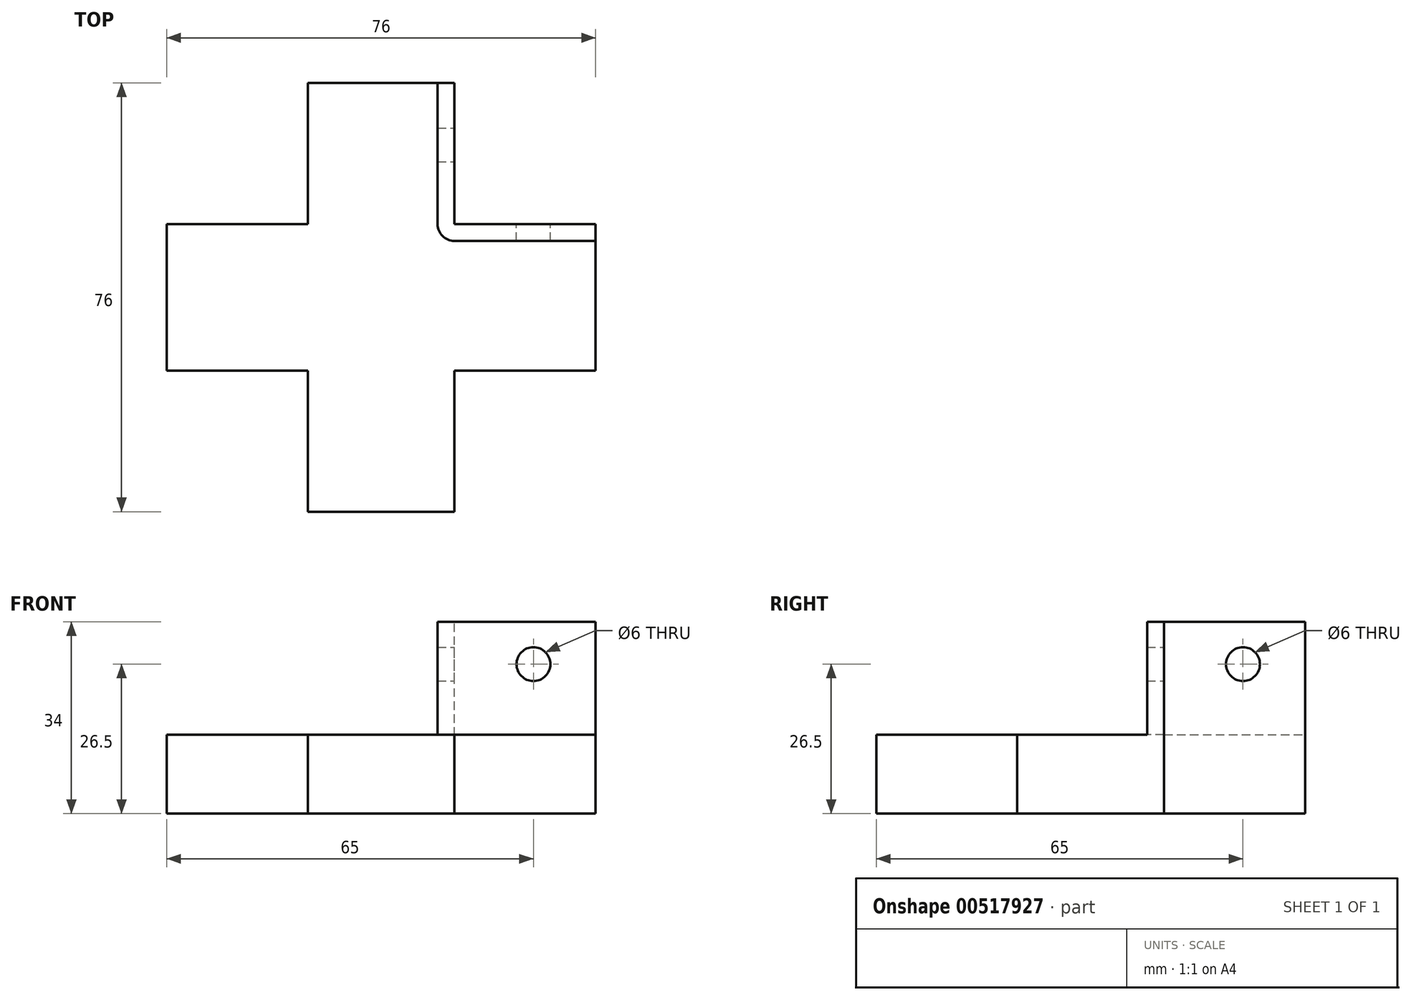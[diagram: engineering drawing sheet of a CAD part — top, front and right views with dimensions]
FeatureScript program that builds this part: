
annotation { "Feature Type Name" : "Feature", "Feature Type Description" : "" }
export const myFeature = defineFeature(function(context is Context, id is Id, definition is map)
    precondition{}
    {
        {
            assignVariable(context, id + "F0", {"name" : "wall_height", "anyValue" : 20});
        }
        {
            var Q0;
            Q0=qCreatedBy(makeId("Top.planeOp"),FACE);
            var sketch = newSketch(context, id + "F1", { "sketchPlane" : qUnion([Q0])});
            skCircle(sketch, "E0", {"center": v(0, 0) * mm, "radius": 15.9 * mm, "construction": true});
            skSolve(sketch);
        }
        {
            var Q0;
            Q0=qCreatedBy(makeId("Top.planeOp"),FACE);
            var sketch = newSketch(context, id + "F2", { "sketchPlane" : qUnion([Q0])});
            skLineSegment(sketch, "E1", {"start": v(-13, 13) * mm, "end": v(-13, 38) * mm});
            skLineSegment(sketch, "E2", {"start": v(-13, 38) * mm, "end": v(13, 38) * mm});
            skLineSegment(sketch, "E3", {"start": v(13, 38) * mm, "end": v(13, 13) * mm});
            skLineSegment(sketch, "E4.1.0", {"start": v(-13, -13) * mm, "end": v(-38, -13) * mm});
            skLineSegment(sketch, "E4.1.1", {"start": v(-38, -13) * mm, "end": v(-38, 13) * mm});
            skLineSegment(sketch, "E4.1.2", {"start": v(-38, 13) * mm, "end": v(-13, 13) * mm});
            skLineSegment(sketch, "E4.2.0", {"start": v(13, -13) * mm, "end": v(13, -38) * mm});
            skLineSegment(sketch, "E4.2.1", {"start": v(13, -38) * mm, "end": v(-13, -38) * mm});
            skLineSegment(sketch, "E4.2.2", {"start": v(-13, -38) * mm, "end": v(-13, -13) * mm});
            skLineSegment(sketch, "E4.3.0", {"start": v(13, 13) * mm, "end": v(38, 13) * mm});
            skLineSegment(sketch, "E4.3.1", {"start": v(38, 13) * mm, "end": v(38, -13) * mm});
            skLineSegment(sketch, "E4.3.2", {"start": v(38, -13) * mm, "end": v(13, -13) * mm});
            skPoint(sketch, "E4.center", {"position": v(0, 0) * mm});
            skSolve(sketch);
        }
        {
            var Q0;
            Q0 = qSketchRegion(id + "F2", true);
            extrude(context, id + "F3", {"entities" : qUnion([Q0]), "oppositeDirection" : true, "depth" : 14 * mm, "offsetDistance" : 25 * mm});
        }
        {
            var Q0;
            Q0=qCreatedBy(makeId("Top.planeOp"),FACE);
            var sketch = newSketch(context, id + "F4", { "sketchPlane" : qUnion([Q0])});
            skLineSegment(sketch, "E5", {"start": v(10, 38) * mm, "end": v(10, 10) * mm});
            skLineSegment(sketch, "E6", {"start": v(10, 10) * mm, "end": v(38, 10) * mm});
            skLineSegment(sketch, "E7.0", {"start": v(13, 13) * mm, "end": v(38, 13) * mm});
            skLineSegment(sketch, "E7.1", {"start": v(13, 38) * mm, "end": v(13, 13) * mm});
            skLineSegment(sketch, "E8", {"start": v(10, 38) * mm, "end": v(13, 38) * mm});
            skLineSegment(sketch, "E9", {"start": v(38, 13) * mm, "end": v(38, 10) * mm});
            skPoint(sketch, "E10.center", {"position": v(0, 0) * mm});
            skSolve(sketch);
        }
        {
            var Q0;
            Q0 = qSketchRegion(id + "F4", true);
            extrude(context, id + "F5", {"entities" : qUnion([Q0]), "operationType" : NewBodyOperationType.ADD, "depth" : (getVariable(context, 'wall_height')) * mm, "offsetDistance" : 25 * mm});
        }
        {
            var Q0;
            Q0=makeQuery(id+"F5.opExtrude","SWEPT_FACE",FACE,{"disambiguationData":[OSD([sQuery(id+"F4.wireOp",EDGE,"E7.0")])]});
            var sketch = newSketch(context, id + "F6", { "sketchPlane" : qUnion([Q0])});
            skPoint(sketch, "E11", {"position": v(-27, 12.5) * mm});
            skSolve(sketch);
        }
        {
            var Q0;
            Q0=makeQuery(id+"F5.opExtrude","SWEPT_FACE",FACE,{"disambiguationData":[OSD([sQuery(id+"F4.wireOp",EDGE,"E7.1")])]});
            var sketch = newSketch(context, id + "F7", { "sketchPlane" : qUnion([Q0])});
            skPoint(sketch, "E12", {"position": v(27, 12.5) * mm});
            skSolve(sketch);
        }
        {
            var Q0;
            Q0=sQuery(id+"F7.wireOp",VERTEX,"E12");
            var Q1;
            Q1=sQuery(id+"F6.wireOp",VERTEX,"E11");
            var Q2;
            Q2=makeQuery(id+"F3.opExtrude","SWEPT_BODY",BODY,{"disambiguationData":[OSD([sQuery(id+"F2.wireOp",EDGE,"E1"),sQuery(id+"F2.wireOp",EDGE,"E2"),sQuery(id+"F2.wireOp",EDGE,"E3"),sQuery(id+"F2.wireOp",EDGE,"E4.1.0"),sQuery(id+"F2.wireOp",EDGE,"E4.1.1"),sQuery(id+"F2.wireOp",EDGE,"E4.1.2"),sQuery(id+"F2.wireOp",EDGE,"E4.2.0"),sQuery(id+"F2.wireOp",EDGE,"E4.2.1"),sQuery(id+"F2.wireOp",EDGE,"E4.2.2"),sQuery(id+"F2.wireOp",EDGE,"E4.3.0"),sQuery(id+"F2.wireOp",EDGE,"E4.3.1"),sQuery(id+"F2.wireOp",EDGE,"E4.3.2")])]});
            hole(context, id + "F8", {"style" : HoleStyle.SIMPLE, "endStyle" : HoleEndStyle.BLIND, "holeDiameter" : 6 * mm, "holeDepth" : 3 * mm, "isTappedThrough" : true, "tappedDepth" : 12 * mm, "tapClearance" : 3, "locations" : qUnion([Q0, Q1]), "scope" : qUnion([Q2])});
        }
        {
            var Q0;
            Q0=makeQuery(id+"F5.opExtrude","SWEPT_EDGE",EDGE,{"disambiguationData":[OSD([sQuery(id+"F4.wireOp",EDGE,"E5"),sQuery(id+"F4.wireOp",EDGE,"E6")])]});
            fillet(context, id + "F9", {"entities" : qUnion([Q0]), "radius" : 3 * mm, "tangentPropagation" : true, "allowEdgeOverflow" : false});
        }
    });
